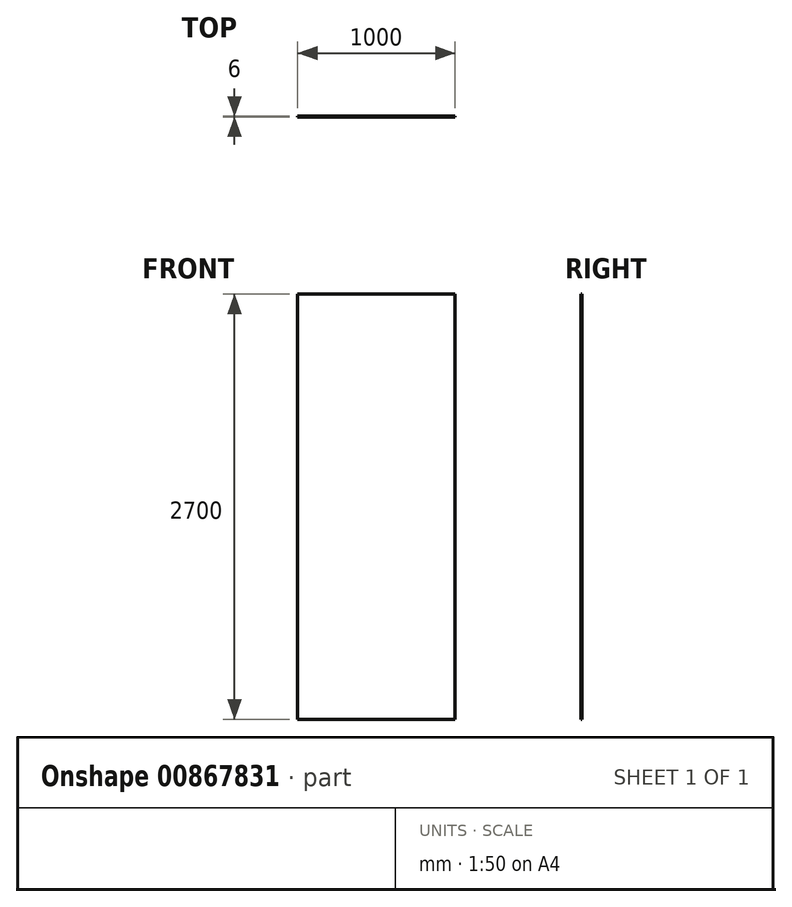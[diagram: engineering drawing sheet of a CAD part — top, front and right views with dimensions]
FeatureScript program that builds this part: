
annotation { "Feature Type Name" : "Feature", "Feature Type Description" : "" }
export const myFeature = defineFeature(function(context is Context, id is Id, definition is map)
    precondition{}
    {
        {
            var Q0;
            Q0=qCreatedBy(makeId("Front.planeOp"),FACE);
            var sketch = newSketch(context, id + "F0", { "sketchPlane" : qUnion([Q0])});
            skLineSegment(sketch, "E0.bottom", {"start": v(-500, 1350) * mm, "end": v(500, 1350) * mm});
            skLineSegment(sketch, "E0.top", {"start": v(-500, -1350) * mm, "end": v(500, -1350) * mm});
            skLineSegment(sketch, "E0.left", {"start": v(-500, 1350) * mm, "end": v(-500, -1350) * mm});
            skLineSegment(sketch, "E0.right", {"start": v(500, 1350) * mm, "end": v(500, -1350) * mm});
            skPoint(sketch, "E0.middle", {"position": v(0, 0) * mm});
            skSolve(sketch);
        }
        {
            var Q0;
            Q0=makeQuery(id+"F0.imprint","IMPRINT",FACE,{"disambiguationData":[TD([[makeQuery(id+"F0.imprint","IMPRINT",EDGE,{"derivedFrom":sQuery(id+"F0.wireOp",EDGE,"E0.bottom")}),-1.0]])]});
            extrude(context, id + "F1", {"entities" : qUnion([Q0]), "depth" : 6 * mm, "offsetDistance" : 25 * mm});
        }
    });
